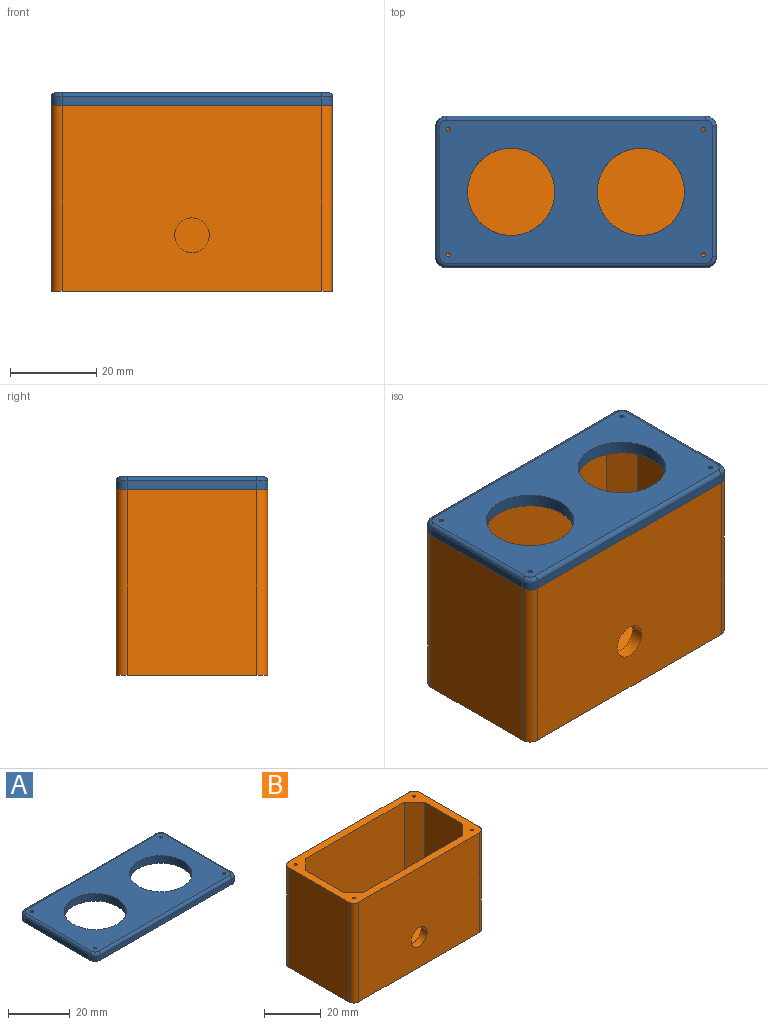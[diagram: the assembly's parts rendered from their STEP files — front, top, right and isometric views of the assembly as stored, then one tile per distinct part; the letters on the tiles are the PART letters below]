
ASSEMBLY  parts=2 mates=1
PART A: 24 faces, bbox 65.4x35.4x3 mm
  f0: plane 30x2mm, normal (-1,0,0), area 60mm2, adj f5,f8,f11,f17
  f1: plane 60x2mm, normal (0,-1,0), area 120mm2, adj f5,f8,f9,f18
  f2: plane 30x2mm, normal (1,0,0), area 60mm2, adj f5,f9,f10,f14
  f3: plane 60x2mm, normal (0,1,0), area 120mm2, adj f5,f10,f11,f13
  f4: plane 63x33mm, normal (0,0,1), area 1433mm2, adj f6,f7,f12,f13,f14,f15,f16,f17
  f5: plane 65x35mm, normal (0,0,-1), area 1625.5mm2, adj f0,f1,f2,f3,f6,f7,f8,f9
  f6: cylinder r=10.1mm len=20.2mm, axis (0,0,-1), area 190.4mm2, adj f4,f5
  f7: cylinder r=10.1mm len=20.2mm, axis (0,0,-1), area 190.4mm2, adj f4,f5
  f8: cylinder r=2.5mm len=2.5mm, axis (0,0,1), area 7.9mm2, adj f0,f1,f5,f19
  f9: cylinder r=2.5mm len=2.5mm, axis (0,0,-1), area 7.9mm2, adj f1,f2,f5,f16
  f10: cylinder r=2.5mm len=2.5mm, axis (0,0,1), area 7.9mm2, adj f2,f3,f5,f12
  f11: cylinder r=2.5mm len=2.5mm, axis (0,0,-1), area 7.9mm2, adj f0,f3,f5,f15
  f12: torus R=1.5mm, axis (0,0,1), area 5.3mm2, adj f4,f10,f13,f14
  f13: cylinder r=1mm len=60mm, axis (1,0,0), area 94.2mm2, adj f3,f4,f12,f15
  f14: cylinder r=1mm len=30mm, axis (0,-1,0), area 47.1mm2, adj f2,f4,f12,f16
  f15: torus R=1.5mm, axis (0,0,1), area 5.3mm2, adj f4,f11,f13,f17
  f16: torus R=1.5mm, axis (0,0,1), area 5.3mm2, adj f4,f9,f14,f18
  f17: cylinder r=1mm len=30mm, axis (0,1,0), area 47.1mm2, adj f0,f4,f15,f19
  f18: cylinder r=1mm len=60mm, axis (-1,0,0), area 94.2mm2, adj f1,f4,f16,f19
  f19: torus R=1.5mm, axis (0,0,1), area 5.3mm2, adj f4,f8,f17,f18
  f20: cylinder r=0.5mm len=3mm, axis (0,0,-1), area 9.4mm2, adj f4,f5
  f21: cylinder r=0.5mm len=3mm, axis (0,0,-1), area 9.4mm2, adj f4,f5
  f22: cylinder r=0.5mm len=3mm, axis (0,0,-1), area 9.4mm2, adj f4,f5
  f23: cylinder r=0.5mm len=3mm, axis (0,0,-1), area 9.4mm2, adj f4,f5
PART B: 29 faces, bbox 65x35x43 mm
  f0: plane 65x35mm, normal (0,0,1), area 605.5mm2, adj f1,f2,f3,f4,f6,f7,f8,f9
  f1: plane 43x30mm, normal (1,0,0), area 1290mm2, adj f0,f5,f11,f14
  f2: plane 60x43mm, normal (0,1,0), area 2580mm2, adj f0,f5,f11,f12
  f3: plane 43x30mm, normal (-1,0,0), area 1290mm2, adj f0,f5,f12,f13
  f4: plane 60x43mm, normal (0,-1,0), area 2529.7mm2, adj f0,f5,f13,f14,f27
  f5: plane 65x35mm, normal (0,0,-1), area 2266.5mm2, adj f1,f2,f3,f4,f11,f12,f13,f14
  f6: plane 40x19mm, normal (-1,0,0), area 760mm2, adj f0,f10,f15,f16
  f7: plane 49x40mm, normal (0,-1,0), area 1960mm2, adj f0,f10,f16,f18
  f8: plane 40x19mm, normal (1,0,0), area 760mm2, adj f0,f10,f17,f18
  f9: plane 49x40mm, normal (0,1,0), area 1909.7mm2, adj f0,f10,f15,f17,f27
  f10: plane 59x29mm, normal (0,0,1), area 1657.9mm2, adj f6,f7,f8,f9,f15,f16,f17,f18
  f11: cylinder r=2.5mm len=43mm, axis (0,0,1), area 168.9mm2, adj f0,f1,f2,f5
  f12: cylinder r=2.5mm len=43mm, axis (0,0,-1), area 168.9mm2, adj f0,f2,f3,f5
  f13: cylinder r=2.5mm len=43mm, axis (0,0,1), area 168.9mm2, adj f0,f3,f4,f5
  f14: cylinder r=2.5mm len=43mm, axis (0,0,-1), area 168.9mm2, adj f0,f1,f4,f5
  f15: plane 40x5mm, normal (-0.71,0.71,0), area 282.8mm2, adj f0,f6,f9,f10
  f16: plane 40x5mm, normal (-0.71,-0.71,0), area 282.8mm2, adj f0,f6,f7,f10
  f17: plane 40x5mm, normal (0.71,0.71,0), area 282.8mm2, adj f0,f8,f9,f10
  f18: plane 40x5mm, normal (0.71,-0.71,0), area 282.8mm2, adj f0,f7,f8,f10
  f19: cone r=0mm half-angle=59deg, axis (0,0,1), area 0.9mm2, adj f20
  f20: cylinder r=0.5mm len=10mm, axis (0,0,1), area 31.4mm2, adj f0,f19
  f21: cone r=0mm half-angle=59deg, axis (0,0,1), area 0.9mm2, adj f22
  f22: cylinder r=0.5mm len=10mm, axis (0,0,1), area 31.4mm2, adj f0,f21
  f23: cone r=0mm half-angle=59deg, axis (0,0,1), area 0.9mm2, adj f24
  f24: cylinder r=0.5mm len=10mm, axis (0,0,1), area 31.4mm2, adj f0,f23
  f25: cone r=0mm half-angle=59deg, axis (0,0,1), area 0.9mm2, adj f26
  f26: cylinder r=0.5mm len=10mm, axis (0,0,1), area 31.4mm2, adj f0,f25
  f27: cylinder r=4mm len=8mm, axis (0,-1,0), area 75.4mm2, adj f4,f9
  f28: cylinder r=1mm len=3mm, axis (0,0,-1), area 18.8mm2, adj f5,f10
PLACE A t=(0,-41.95,40)mm
PLACE B t=(0,0,-3)mm
MATE planar A.f5 <-> B.f0  axis (0,0,-1) through (0,-41.95,40)mm
